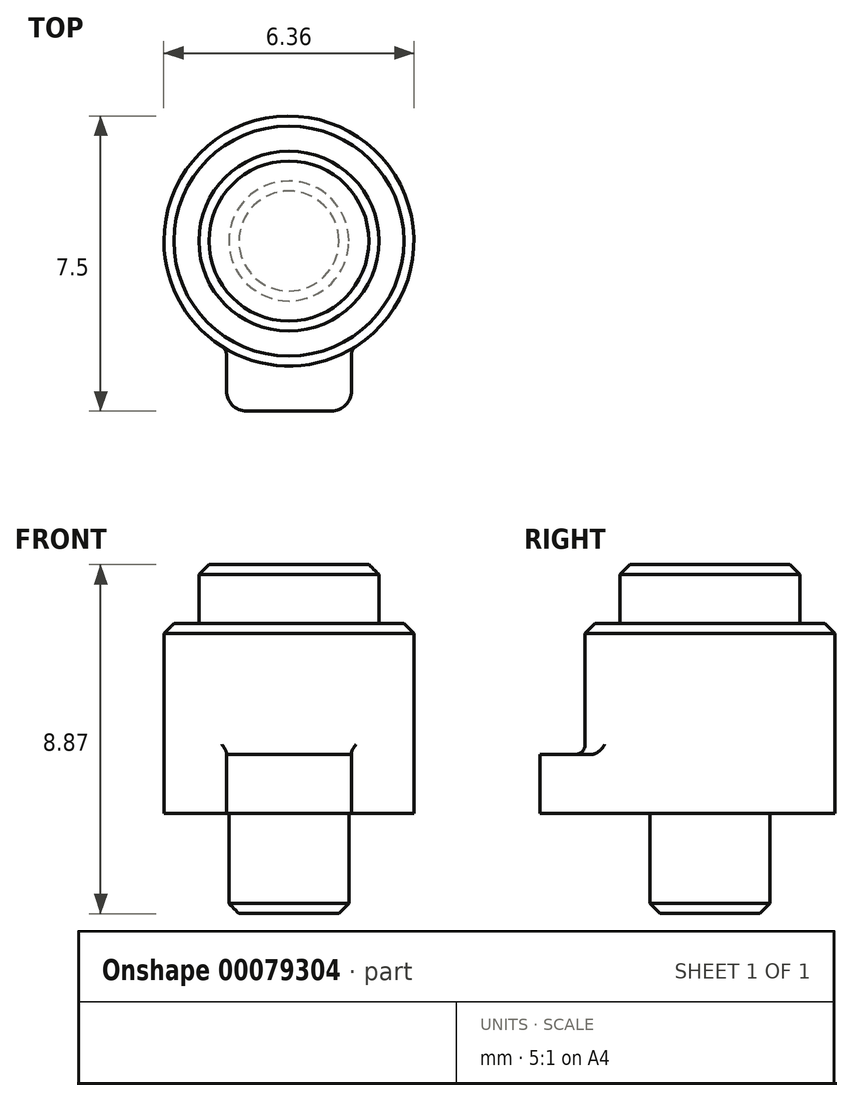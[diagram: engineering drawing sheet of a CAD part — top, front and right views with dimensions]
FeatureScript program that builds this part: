
annotation { "Feature Type Name" : "Feature", "Feature Type Description" : "" }
export const myFeature = defineFeature(function(context is Context, id is Id, definition is map)
    precondition{}
    {
        {
            var Q0;
            Q0=qCreatedBy(makeId("Top.planeOp"),FACE);
            var sketch = newSketch(context, id + "F0", { "sketchPlane" : qUnion([Q0])});
            skCircle(sketch, "E0", {"center": v(0, 0) * mm, "radius": 2.29 * mm});
            skSolve(sketch);
        }
        {
            var Q0;
            Q0=makeQuery(id+"F0.imprint","IMPRINT",FACE,{"disambiguationData":[TD([[makeQuery(id+"F0.imprint","IMPRINT",EDGE,{"derivedFrom":sQuery(id+"F0.wireOp",EDGE,"E0")}),1.0]])]});
            extrude(context, id + "F1", {"entities" : qUnion([Q0]), "depth" : 1.5 * mm});
        }
        {
            var Q0;
            Q0=makeQuery(id+"F1.opExtrude","CAP_FACE",FACE,{"disambiguationData":[OSD([sQuery(id+"F0.wireOp",EDGE,"E0")])],"isStart":true});
            var sketch = newSketch(context, id + "F2", { "sketchPlane" : qUnion([Q0])});
            skCircle(sketch, "E1", {"center": v(0, 0) * mm, "radius": 3.18 * mm});
            skSolve(sketch);
        }
        {
            var Q0;
            Q0=makeQuery(id+"F2.imprint","IMPRINT",FACE,{"disambiguationData":[TD([[makeQuery(id+"F2.imprint","IMPRINT",EDGE,{"derivedFrom":makeQuery(id+"F1.opExtrude","CAP_EDGE",EDGE,{"disambiguationData":[OSD([sQuery(id+"F0.wireOp",EDGE,"E0")])],"isStart":true})}),-1.0]])]});
            var Q1;
            Q1=makeQuery(id+"F2.imprint","IMPRINT",FACE,{"disambiguationData":[TD([[makeQuery(id+"F2.imprint","IMPRINT",EDGE,{"derivedFrom":sQuery(id+"F2.wireOp",EDGE,"E1")}),1.0]])]});
            extrude(context, id + "F3", {"entities" : qUnion([Q0, Q1]), "operationType" : NewBodyOperationType.ADD, "depth" : 4.83 * mm});
        }
        {
            var Q0;
            Q0=makeQuery(id+"F1.opExtrude","CAP_EDGE",EDGE,{"disambiguationData":[OSD([sQuery(id+"F0.wireOp",EDGE,"E0")])],"isStart":false});
            chamfer(context, id + "F4", {"entities" : qUnion([Q0]), "width" : 0.25 * mm, "tangentPropagation" : true});
        }
        {
            var Q0;
            Q0=makeQuery(id+"F3.opExtrude","CAP_FACE",FACE,{"disambiguationData":[OSD([sQuery(id+"F2.wireOp",EDGE,"E1")])],"isStart":false});
            var sketch = newSketch(context, id + "F5", { "sketchPlane" : qUnion([Q0])});
            skCircle(sketch, "E2", {"center": v(0, 0) * mm, "radius": 1.52 * mm});
            skSolve(sketch);
        }
        {
            var Q0;
            Q0=makeQuery(id+"F5.imprint","IMPRINT",FACE,{"disambiguationData":[TD([[makeQuery(id+"F5.imprint","IMPRINT",EDGE,{"derivedFrom":sQuery(id+"F5.wireOp",EDGE,"0xtLJy08-jNCn-ZhcF-ebt5-pMlnsXQ1GP0J")}),1.0]])]});
            var Q1;
            Q1=makeQuery(id+"F5.imprint","IMPRINT",FACE,{"disambiguationData":[TD([[makeQuery(id+"F5.imprint","IMPRINT",EDGE,{"derivedFrom":sQuery(id+"F5.wireOp",EDGE,"E2")}),1.0]])]});
            extrude(context, id + "F6", {"entities" : qUnion([Q0, Q1]), "operationType" : NewBodyOperationType.ADD, "depth" : 2.54 * mm});
        }
        {
            var Q0;
            Q0=qCreatedBy(makeId("Front.planeOp"),FACE);
            var sketch = newSketch(context, id + "F7", { "sketchPlane" : qUnion([Q0])});
            skLineSegment(sketch, "E3.0", {"start": v(3.18, -4.83) * mm, "end": v(-3.18, -4.83) * mm, "construction": true});
            skLineSegment(sketch, "E4", {"start": v(-3.18, -4.83) * mm, "end": v(-3.18, -3.33) * mm, "construction": true});
            skLineSegment(sketch, "E5", {"start": v(-3.18, -3.33) * mm, "end": v(3.18, -3.33) * mm, "construction": true});
            skLineSegment(sketch, "E6", {"start": v(3.18, -3.33) * mm, "end": v(3.18, -4.83) * mm, "construction": true});
            skLineSegment(sketch, "E7.bottom", {"start": v(-1.59, -3.33) * mm, "end": v(1.59, -3.33) * mm});
            skLineSegment(sketch, "E7.top", {"start": v(-1.59, -4.83) * mm, "end": v(1.59, -4.83) * mm});
            skLineSegment(sketch, "E7.left", {"start": v(-1.59, -3.33) * mm, "end": v(-1.59, -4.83) * mm});
            skLineSegment(sketch, "E7.right", {"start": v(1.59, -3.33) * mm, "end": v(1.59, -4.83) * mm});
            skSolve(sketch);
        }
        {
            var Q0;
            Q0 = qSketchRegion(id + "F7", true);
            extrude(context, id + "F8", {"entities" : qUnion([Q0]), "operationType" : NewBodyOperationType.ADD, "depth" : 4.32 * mm});
        }
        {
            var Q0;
            Q0=makeQuery(id+"F8.opExtrude","CAP_EDGE",EDGE,{"disambiguationData":[OSD([sQuery(id+"F7.wireOp",EDGE,"E7.left")])],"isStart":false});
            var Q1;
            Q1=makeQuery(id+"F8.opExtrude","CAP_EDGE",EDGE,{"disambiguationData":[OSD([sQuery(id+"F7.wireOp",EDGE,"E7.right")])],"isStart":false});
            fillet(context, id + "F9", {"entities" : qUnion([Q0, Q1]), "radius" : 0.5 * mm, "tangentPropagation" : true, "allowEdgeOverflow" : false});
        }
        {
            var Q0;
            Q0=makeQuery(id+"F6.opExtrude","CAP_EDGE",EDGE,{"disambiguationData":[OSD([sQuery(id+"F5.wireOp",EDGE,"E2")])],"isStart":false});
            chamfer(context, id + "F10", {"entities" : qUnion([Q0]), "width" : 0.25 * mm, "tangentPropagation" : true});
        }
        {
            var Q0;
            Q0=makeQuery(id+"F8.boolean.opBoolean","INTERSECT",EDGE,{"derivedFrom":[makeQuery(id+"F3.opExtrude","SWEPT_FACE",FACE,{"disambiguationData":[OSD([sQuery(id+"F2.wireOp",EDGE,"E1")])]}),makeQuery(id+"F8.opExtrude","SWEPT_FACE",FACE,{"disambiguationData":[OSD([sQuery(id+"F7.wireOp",EDGE,"E7.bottom")])]})]});
            var Q1;
            Q1=makeQuery(id+"F8.boolean.opBoolean","INTERSECT",EDGE,{"derivedFrom":[makeQuery(id+"F3.opExtrude","SWEPT_FACE",FACE,{"disambiguationData":[OSD([sQuery(id+"F2.wireOp",EDGE,"E1")])]}),makeQuery(id+"F8.opExtrude","SWEPT_FACE",FACE,{"disambiguationData":[OSD([sQuery(id+"F7.wireOp",EDGE,"E7.right")])]})]});
            var Q2;
            Q2=makeQuery(id+"F8.boolean.opBoolean","INTERSECT",EDGE,{"derivedFrom":[makeQuery(id+"F3.opExtrude","SWEPT_FACE",FACE,{"disambiguationData":[OSD([sQuery(id+"F2.wireOp",EDGE,"E1")])]}),makeQuery(id+"F8.opExtrude","SWEPT_FACE",FACE,{"disambiguationData":[OSD([sQuery(id+"F7.wireOp",EDGE,"E7.left")])]})]});
            fillet(context, id + "F11", {"entities" : qUnion([Q0, Q1, Q2]), "radius" : 0.25 * mm, "tangentPropagation" : true, "allowEdgeOverflow" : false});
        }
        {
            var Q0;
            Q0=makeQuery(id+"F3.opExtrude","CAP_EDGE",EDGE,{"disambiguationData":[OSD([sQuery(id+"F2.wireOp",EDGE,"E1")])],"isStart":true});
            chamfer(context, id + "F12", {"entities" : qUnion([Q0]), "width" : 0.25 * mm});
        }
    });
